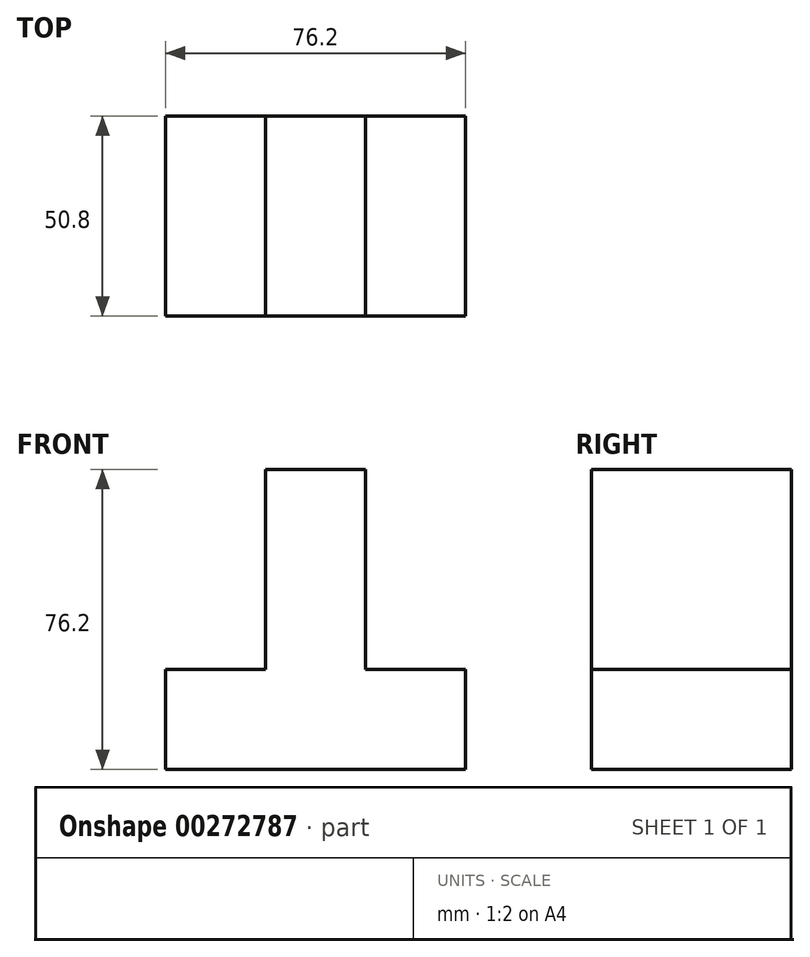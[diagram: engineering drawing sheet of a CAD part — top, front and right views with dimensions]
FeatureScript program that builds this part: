
annotation { "Feature Type Name" : "Feature", "Feature Type Description" : "" }
export const myFeature = defineFeature(function(context is Context, id is Id, definition is map)
    precondition{}
    {
        {
            var Q0;
            Q0=qCreatedBy(makeId("Front.planeOp"),FACE);
            var sketch = newSketch(context, id + "F0", { "sketchPlane" : qUnion([Q0])});
            skPoint(sketch, "E0.end.orphan", {"position": v(0, 25.4) * mm});
            skLineSegment(sketch, "E1", {"start": v(0, 0) * mm, "end": v(-76.2, 0) * mm});
            skLineSegment(sketch, "E2", {"start": v(-76.2, 0) * mm, "end": v(-76.2, 25.4) * mm});
            skLineSegment(sketch, "E3", {"start": v(0, 25.4) * mm, "end": v(0, 0) * mm});
            skPoint(sketch, "E4.start.orphan", {"position": v(-25.4, 25.4) * mm});
            skLineSegment(sketch, "E5", {"start": v(-76.2, 25.4) * mm, "end": v(-50.8, 25.4) * mm});
            skLineSegment(sketch, "E6", {"start": v(-50.8, 25.4) * mm, "end": v(-50.8, 76.2) * mm});
            skLineSegment(sketch, "E7", {"start": v(-50.8, 76.2) * mm, "end": v(-25.4, 76.2) * mm});
            skLineSegment(sketch, "E8", {"start": v(-25.4, 76.2) * mm, "end": v(-25.4, 25.4) * mm});
            skLineSegment(sketch, "E9", {"start": v(-25.4, 25.4) * mm, "end": v(0, 25.4) * mm});
            skSolve(sketch);
        }
        {
            var Q0;
            Q0 = qSketchRegion(id + "F0", true);
            extrude(context, id + "F1", {"entities" : qUnion([Q0]), "depth" : 50.8 * mm});
        }
    });
